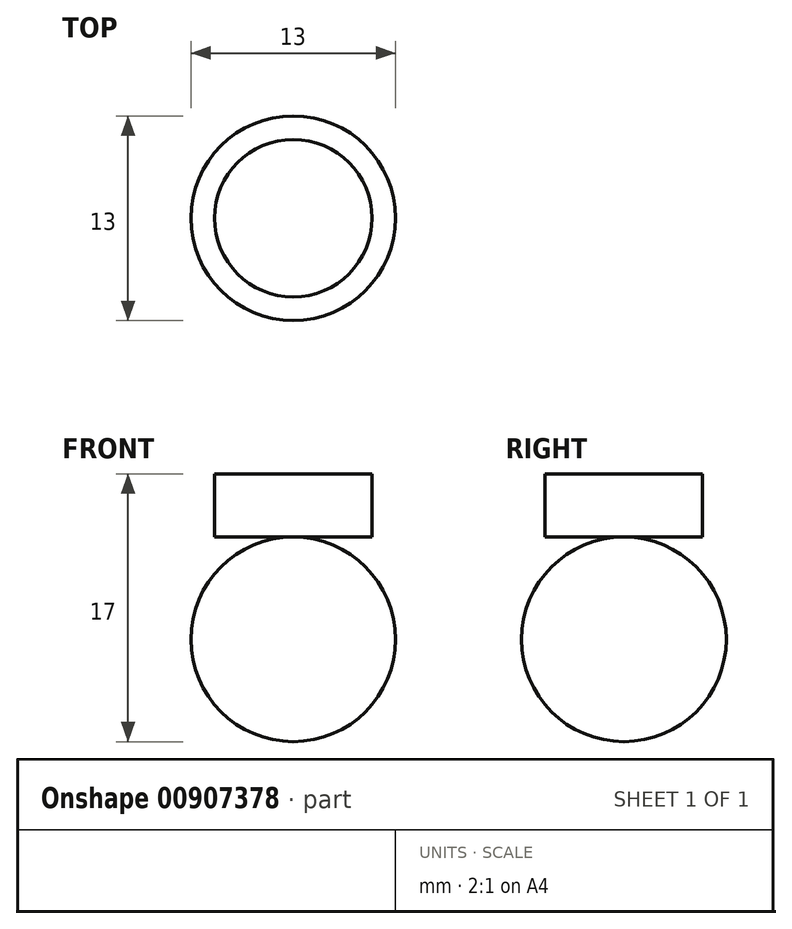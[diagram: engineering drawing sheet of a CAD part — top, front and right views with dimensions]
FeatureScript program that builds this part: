
annotation { "Feature Type Name" : "Feature", "Feature Type Description" : "" }
export const myFeature = defineFeature(function(context is Context, id is Id, definition is map)
    precondition{}
    {
        {
            var Q0;
            Q0=qCreatedBy(makeId("Front.planeOp"),FACE);
            var sketch = newSketch(context, id + "F0", { "sketchPlane" : qUnion([Q0])});
            skArc(sketch, "E0", {"start": v(0, -6.5) * mm, "mid": v(6.5, 0) * mm, "end": v(0, 6.5) * mm});
            skLineSegment(sketch, "E1", {"start": v(0, 6.5) * mm, "end": v(5, 6.5) * mm});
            skLineSegment(sketch, "E2", {"start": v(5, 6.5) * mm, "end": v(5, 10.5) * mm});
            skLineSegment(sketch, "E3", {"start": v(5, 10.5) * mm, "end": v(0, 10.5) * mm});
            skLineSegment(sketch, "E4", {"start": v(0, 10.5) * mm, "end": v(0, 6.5) * mm});
            skLineSegment(sketch, "E5", {"start": v(0, 6.5) * mm, "end": v(0, -6.5) * mm});
            skSolve(sketch);
        }
        {
            var Q0;
            Q0 = qSketchRegion(id + "F0", true);
            var Q1;
            Q1=sQuery(id+"F0.wireOp",EDGE,"E5");
            revolve(context, id + "F1", {"surfaceOperationType" : NewSurfaceOperationType.NEW, "entities" : qUnion([Q0]), "axis" : qUnion([Q1]), "revolveType" : RevolveType.FULL});
        }
    });
